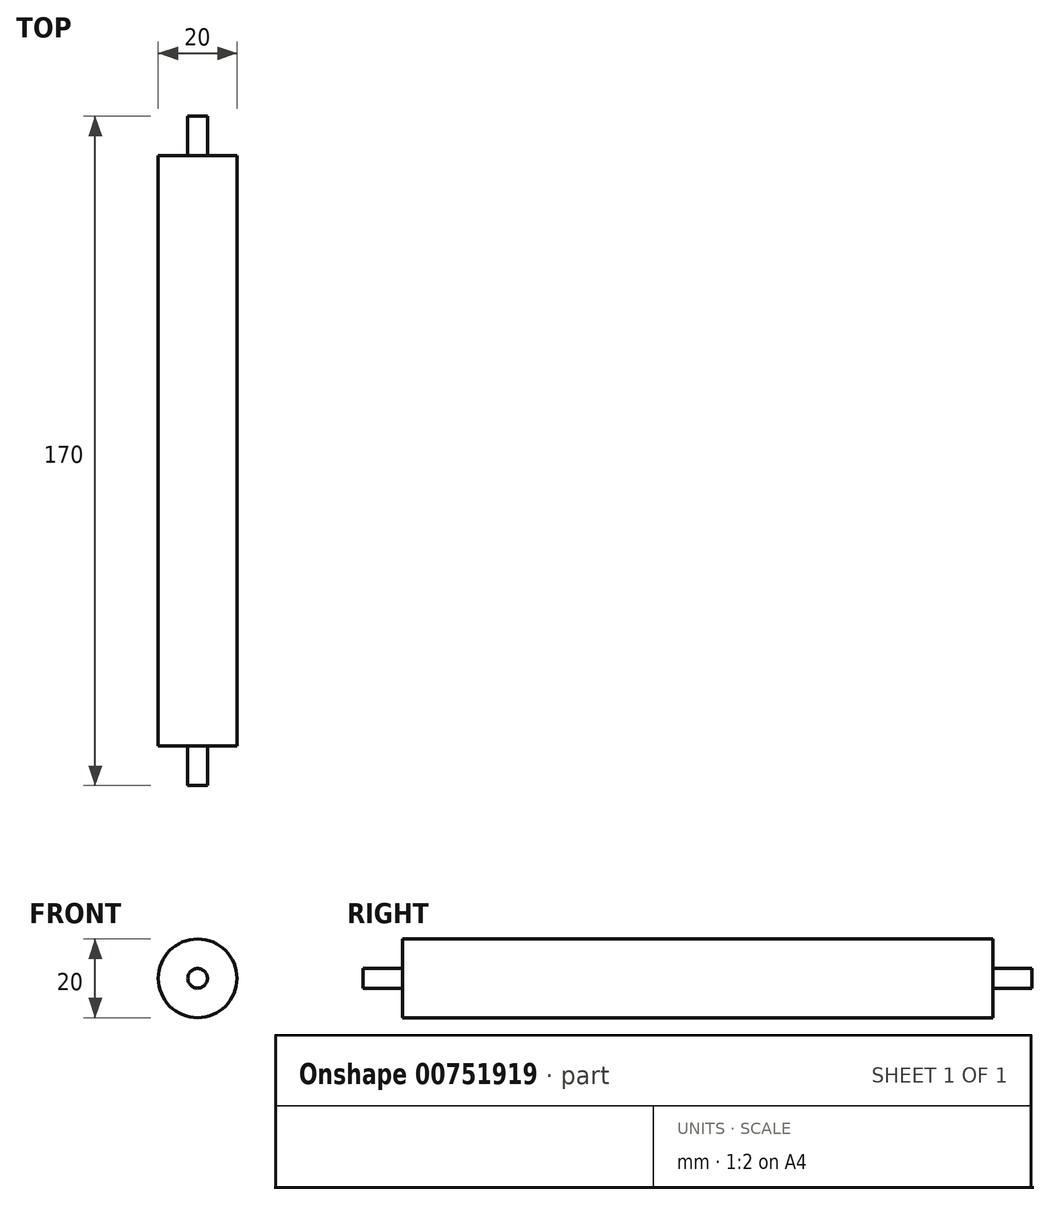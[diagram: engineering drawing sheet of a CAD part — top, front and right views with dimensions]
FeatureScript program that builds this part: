
annotation { "Feature Type Name" : "Feature", "Feature Type Description" : "" }
export const myFeature = defineFeature(function(context is Context, id is Id, definition is map)
    precondition{}
    {
        {
            var Q0;
            Q0=qCreatedBy(makeId("Front.planeOp"),FACE);
            var sketch = newSketch(context, id + "F0", { "sketchPlane" : qUnion([Q0])});
            skCircle(sketch, "E0", {"center": v(0, 0) * mm, "radius": 10 * mm});
            skSolve(sketch);
        }
        {
            var Q0;
            Q0 = qSketchRegion(id + "F0", true);
            extrude(context, id + "F1", {"entities" : qUnion([Q0]), "oppositeDirection" : true, "depth" : 150 * mm, "offsetDistance" : 25 * mm});
        }
        {
            var Q0;
            Q0=makeQuery(id+"F1.opExtrude","CAP_FACE",FACE,{"disambiguationData":[OSD([sQuery(id+"F0.wireOp",EDGE,"E0")])],"isStart":true});
            cPlane(context, id + "F2", {"entities" : qUnion([Q0]), "cplaneType" : CPlaneType.OFFSET, "offset" : 0 * mm, "oppositeDirection" : true, "width" : 150 * mm, "height" : 150 * mm});
        }
        {
            var Q0;
            Q0=qCreatedBy(id+"F2.planeOp",FACE);
            var sketch = newSketch(context, id + "F3", { "sketchPlane" : qUnion([Q0])});
            skCircle(sketch, "E1", {"center": v(0, 0) * mm, "radius": 2.5 * mm});
            skSolve(sketch);
        }
        {
            var Q0;
            Q0=makeQuery(id+"F3.imprint","IMPRINT",FACE,{"disambiguationData":[TD([[makeQuery(id+"F3.imprint","IMPRINT",EDGE,{"derivedFrom":sQuery(id+"F3.wireOp",EDGE,"E1")}),1.0]])]});
            var Q1;
            Q1=sQuery(id+"F3.wireOp",EDGE,"E1");
            extrude(context, id + "F4", {"entities" : qUnion([Q0]), "surfaceEntities" : qUnion([Q1]), "depth" : 10 * mm, "offsetDistance" : 25 * mm});
        }
        {
            var Q0;
            Q0=makeQuery(id+"F1.opExtrude","CAP_FACE",FACE,{"disambiguationData":[OSD([sQuery(id+"F0.wireOp",EDGE,"E0")])],"isStart":false});
            cPlane(context, id + "F5", {"entities" : qUnion([Q0]), "cplaneType" : CPlaneType.OFFSET, "offset" : 0 * mm, "width" : 150 * mm, "height" : 150 * mm});
        }
        {
            var Q0;
            Q0=qCreatedBy(id+"F5.planeOp",FACE);
            var sketch = newSketch(context, id + "F6", { "sketchPlane" : qUnion([Q0])});
            skCircle(sketch, "E2", {"center": v(0, 0) * mm, "radius": 2.5 * mm});
            skSolve(sketch);
        }
        {
            var Q0;
            Q0 = qSketchRegion(id + "F6", true);
            extrude(context, id + "F7", {"entities" : qUnion([Q0]), "operationType" : NewBodyOperationType.ADD, "depth" : 10 * mm, "offsetDistance" : 25 * mm});
        }
    });
